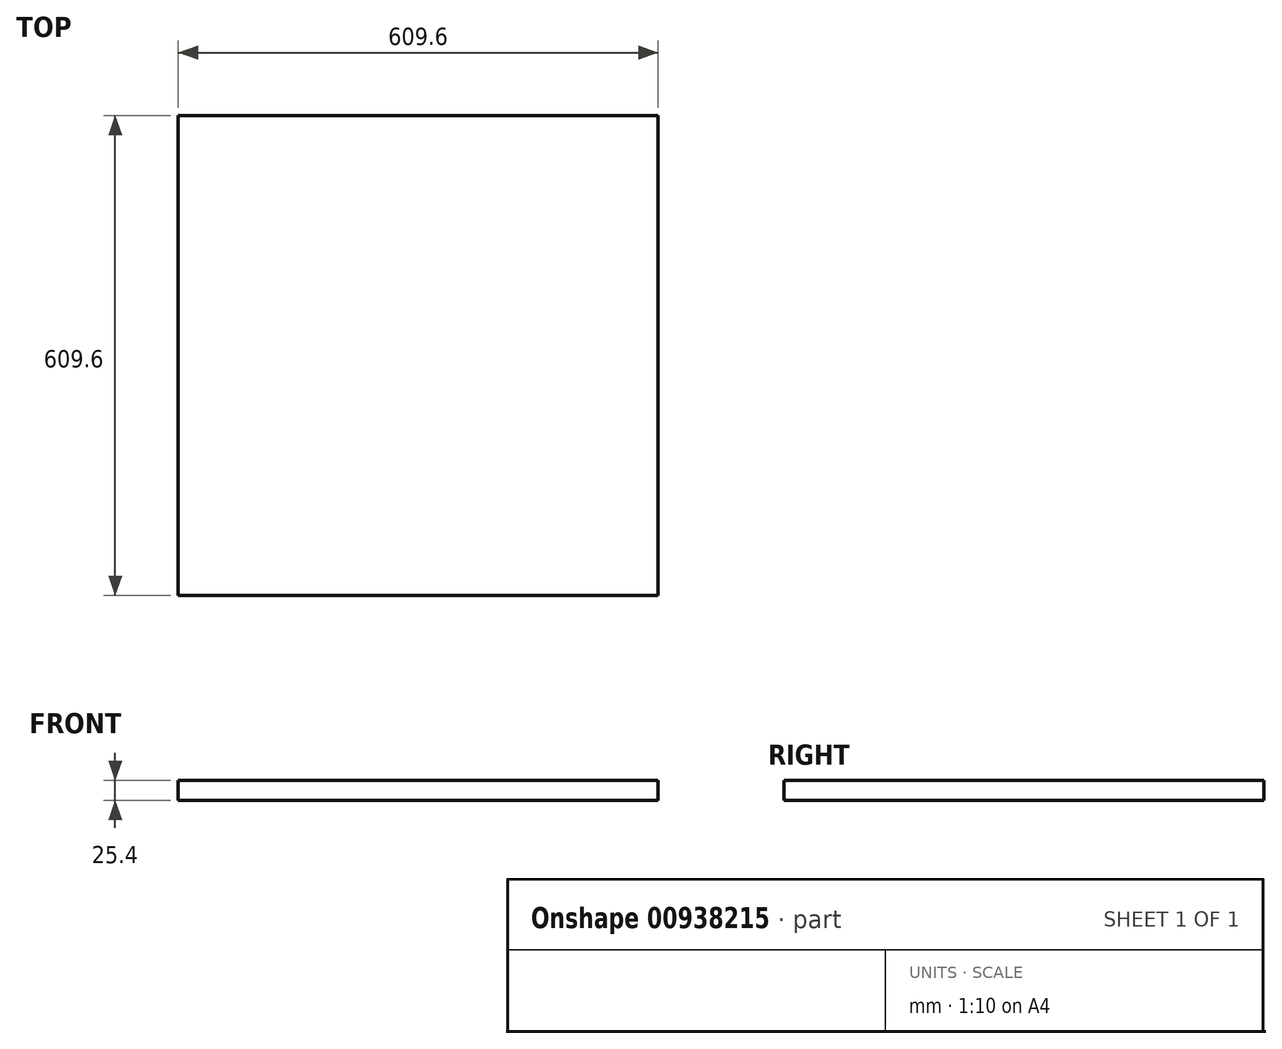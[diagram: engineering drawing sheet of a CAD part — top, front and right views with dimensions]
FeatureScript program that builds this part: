
annotation { "Feature Type Name" : "Feature", "Feature Type Description" : "" }
export const myFeature = defineFeature(function(context is Context, id is Id, definition is map)
    precondition{}
    {
        {
            var Q0;
            Q0=qCreatedBy(makeId("Top.planeOp"),FACE);
            var sketch = newSketch(context, id + "F0", { "sketchPlane" : qUnion([Q0])});
            skLineSegment(sketch, "E0.bottom", {"start": v(304.8, 304.8) * mm, "end": v(-304.8, 304.8) * mm});
            skLineSegment(sketch, "E0.top", {"start": v(304.8, -304.8) * mm, "end": v(-304.8, -304.8) * mm});
            skLineSegment(sketch, "E0.left", {"start": v(304.8, 304.8) * mm, "end": v(304.8, -304.8) * mm});
            skLineSegment(sketch, "E0.right", {"start": v(-304.8, 304.8) * mm, "end": v(-304.8, -304.8) * mm});
            skPoint(sketch, "E0.middle", {"position": v(0, 0) * mm});
            skSolve(sketch);
        }
        {
            var Q0;
            Q0 = qSketchRegion(id + "F0", true);
            extrude(context, id + "F1", {"entities" : qUnion([Q0]), "depth" : 25.4 * mm, "offsetDistance" : 25.4 * mm});
        }
    });
